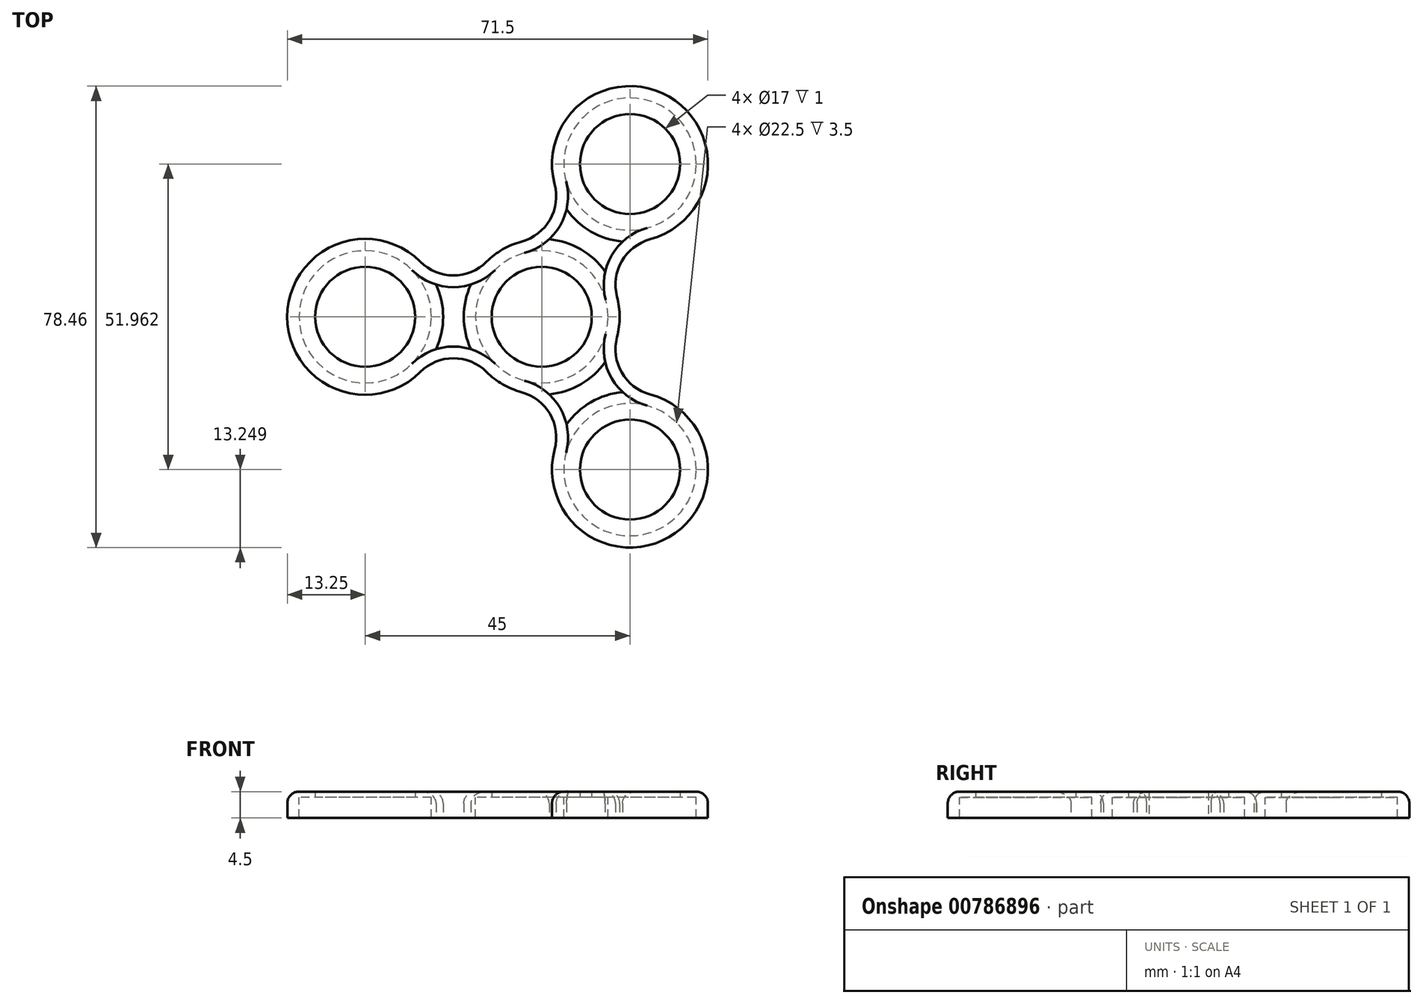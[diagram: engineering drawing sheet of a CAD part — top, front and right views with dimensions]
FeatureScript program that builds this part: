
annotation { "Feature Type Name" : "Feature", "Feature Type Description" : "" }
export const myFeature = defineFeature(function(context is Context, id is Id, definition is map)
    precondition{}
    {
        {
            assignVariable(context, id + "F0", {"name" : "B608_T", "anyValue" : 7});
        }
        {
            var Q0;
            Q0=qCreatedBy(makeId("Top.planeOp"),FACE);
            var sketch = newSketch(context, id + "F1", { "sketchPlane" : qUnion([Q0])});
            skCircle(sketch, "E0", {"center": v(0, 0) * mm, "radius": 11.25 * mm});
            skCircle(sketch, "E1.cCircle", {"center": v(0, 0) * mm, "radius": 15 * mm, "construction": true});
            skLineSegment(sketch, "E1.0", {"start": v(15, 25.98) * mm, "end": v(15, -25.98) * mm, "construction": true});
            skLineSegment(sketch, "E1.1", {"start": v(15, -25.98) * mm, "end": v(-30, 0) * mm, "construction": true});
            skLineSegment(sketch, "E1.2", {"start": v(-30, 0) * mm, "end": v(15, 25.98) * mm, "construction": true});
            skPoint(sketch, "E1.0.midPoint", {"position": v(15, 0) * mm});
            skCircle(sketch, "E2", {"center": v(-30, 0) * mm, "radius": 11.25 * mm});
            skCircle(sketch, "E3", {"center": v(15, -25.98) * mm, "radius": 11.25 * mm});
            skCircle(sketch, "E4", {"center": v(15, 25.98) * mm, "radius": 11.25 * mm});
            skPoint(sketch, "E5.orphan", {"position": v(0, -11.15) * mm});
            skPoint(sketch, "E6.orphan", {"position": v(0, 11.15) * mm});
            skArc(sketch, "E7.0", {"start": v(-17.94, -5.5) * mm, "mid": v(-16.75, 0) * mm, "end": v(-17.94, 5.5) * mm});
            skArc(sketch, "E8.0", {"start": v(2.2, -22.57) * mm, "mid": v(21.62, -37.46) * mm, "end": v(18.45, -13.19) * mm});
            skArc(sketch, "E9.0", {"start": v(18.45, 13.19) * mm, "mid": v(13.9, 39.18) * mm, "end": v(13.73, 12.8) * mm});
            skArc(sketch, "E10.0", {"start": v(-9.35, -9.39) * mm, "mid": v(-6.62, -11.47) * mm, "end": v(-3.45, -12.8) * mm});
            skLineSegment(sketch, "E11", {"start": v(-7.65, -13.25) * mm, "end": v(-7.03, -13.25) * mm});
            skLineSegment(sketch, "E12", {"start": v(-7.65, 13.25) * mm, "end": v(-7.03, 13.25) * mm});
            skLineSegment(sketch, "E13", {"start": v(-7.65, -13.25) * mm, "end": v(-7.96, -12.71) * mm});
            skLineSegment(sketch, "E14", {"start": v(15.3, 0) * mm, "end": v(15, 0.54) * mm});
            skLineSegment(sketch, "E15", {"start": v(-7.96, 12.71) * mm, "end": v(-7.65, 13.25) * mm});
            skLineSegment(sketch, "E16", {"start": v(15, -0.54) * mm, "end": v(15.3, 0) * mm});
            skPoint(sketch, "E17.orphan", {"position": v(0, -13.25) * mm});
            skPoint(sketch, "E18.orphan", {"position": v(0, 13.25) * mm});
            skCircle(sketch, "E19", {"center": v(0, 0) * mm, "radius": 8.5 * mm});
            skCircle(sketch, "E20", {"center": v(-30, 0) * mm, "radius": 8.5 * mm});
            skCircle(sketch, "E21", {"center": v(15, -25.98) * mm, "radius": 8.5 * mm});
            skCircle(sketch, "E22", {"center": v(15, 25.98) * mm, "radius": 8.5 * mm});
            skArc(sketch, "E23", {"start": v(-20.65, 9.39) * mm, "mid": v(-15, 7.05) * mm, "end": v(-9.35, 9.39) * mm});
            skArc(sketch, "E24", {"start": v(-9.35, -9.39) * mm, "mid": v(-15, -7.05) * mm, "end": v(-20.65, -9.39) * mm});
            skArc(sketch, "E25", {"start": v(-3.45, 12.8) * mm, "mid": v(1.4, 16.52) * mm, "end": v(2.2, 22.57) * mm});
            skArc(sketch, "E26", {"start": v(18.45, 13.19) * mm, "mid": v(13.6, 9.46) * mm, "end": v(12.8, 3.4) * mm});
            skArc(sketch, "E27", {"start": v(12.8, -3.4) * mm, "mid": v(13.6, -9.46) * mm, "end": v(18.45, -13.19) * mm});
            skArc(sketch, "E28", {"start": v(2.2, -22.57) * mm, "mid": v(1.4, -16.52) * mm, "end": v(-3.45, -12.8) * mm});
            skPoint(sketch, "E29.orphan", {"position": v(-30, 13.25) * mm});
            skPoint(sketch, "E30.orphan", {"position": v(-30, -13.25) * mm});
            skArc(sketch, "E31.0", {"start": v(-12.06, -5.5) * mm, "mid": v(-15, -5.05) * mm, "end": v(-17.94, -5.5) * mm});
            skArc(sketch, "E32.0", {"start": v(-17.94, 5.5) * mm, "mid": v(-15, 5.05) * mm, "end": v(-12.06, 5.5) * mm});
            skArc(sketch, "E33.trimOffspring", {"start": v(-12.06, 5.5) * mm, "mid": v(-13.25, 0) * mm, "end": v(-12.06, -5.5) * mm});
            skArc(sketch, "E34.trimOffspring", {"start": v(-20.65, 9.39) * mm, "mid": v(-43.25, 0) * mm, "end": v(-20.65, -9.39) * mm});
            skArc(sketch, "E35.trimOffspring", {"start": v(4.21, -18.29) * mm, "mid": v(3.12, -15.52) * mm, "end": v(1.27, -13.19) * mm});
            skArc(sketch, "E36.0", {"start": v(10.79, -7.7) * mm, "mid": v(11.88, -10.46) * mm, "end": v(13.73, -12.8) * mm});
            skArc(sketch, "E37.trimOffspring", {"start": v(1.27, -13.19) * mm, "mid": v(6.63, -11.47) * mm, "end": v(10.79, -7.7) * mm});
            skArc(sketch, "E38.trimOffspring", {"start": v(13.73, -12.8) * mm, "mid": v(8.38, -14.5) * mm, "end": v(4.21, -18.29) * mm});
            skArc(sketch, "E39.trimOffspring", {"start": v(12.8, -3.4) * mm, "mid": v(13.25, 0) * mm, "end": v(12.8, 3.4) * mm});
            skArc(sketch, "E40.0", {"start": v(1.27, 13.19) * mm, "mid": v(3.12, 15.52) * mm, "end": v(4.21, 18.29) * mm});
            skArc(sketch, "E41.trimOffspring", {"start": v(10.79, 7.7) * mm, "mid": v(6.62, 11.47) * mm, "end": v(1.27, 13.19) * mm});
            skArc(sketch, "E42.trimOffspring", {"start": v(13.73, 12.8) * mm, "mid": v(11.88, 10.46) * mm, "end": v(10.79, 7.7) * mm});
            skArc(sketch, "E43.trimOffspring", {"start": v(-3.45, 12.8) * mm, "mid": v(-6.63, 11.47) * mm, "end": v(-9.35, 9.39) * mm});
            skSolve(sketch);
        }
        {
            var Q0;
            Q0=makeQuery(id+"F1.imprint","IMPRINT",FACE,{"disambiguationData":[TD([[makeQuery(id+"F1.imprint","IMPRINT",EDGE,{"derivedFrom":sQuery(id+"F1.wireOp",EDGE,"E10.0")}),-1.0]])]});
            var Q1;
            Q1=makeQuery(id+"F1.imprint","IMPRINT",FACE,{"disambiguationData":[TD([[makeQuery(id+"F1.imprint","IMPRINT",EDGE,{"derivedFrom":sQuery(id+"F1.wireOp",EDGE,"E2")}),-1.0]])]});
            var Q2;
            Q2=makeQuery(id+"F1.imprint","IMPRINT",FACE,{"disambiguationData":[TD([[makeQuery(id+"F1.imprint","IMPRINT",EDGE,{"derivedFrom":sQuery(id+"F1.wireOp",EDGE,"E2")}),1.0]])]});
            var Q3;
            Q3=makeQuery(id+"F1.imprint","IMPRINT",FACE,{"disambiguationData":[TD([[makeQuery(id+"F1.imprint","IMPRINT",EDGE,{"derivedFrom":sQuery(id+"F1.wireOp",EDGE,"E0")}),-1.0]])]});
            var Q4;
            Q4=makeQuery(id+"F1.imprint","IMPRINT",FACE,{"disambiguationData":[TD([[makeQuery(id+"F1.imprint","IMPRINT",EDGE,{"derivedFrom":sQuery(id+"F1.wireOp",EDGE,"E0")}),1.0]])]});
            var Q5;
            Q5=makeQuery(id+"F1.imprint","IMPRINT",FACE,{"disambiguationData":[TD([[makeQuery(id+"F1.imprint","IMPRINT",EDGE,{"derivedFrom":sQuery(id+"F1.wireOp",EDGE,"E4")}),-1.0]])]});
            var Q6;
            Q6=makeQuery(id+"F1.imprint","IMPRINT",FACE,{"disambiguationData":[TD([[makeQuery(id+"F1.imprint","IMPRINT",EDGE,{"derivedFrom":sQuery(id+"F1.wireOp",EDGE,"E4")}),1.0]])]});
            var Q7;
            Q7=makeQuery(id+"F1.imprint","IMPRINT",FACE,{"disambiguationData":[TD([[makeQuery(id+"F1.imprint","IMPRINT",EDGE,{"derivedFrom":sQuery(id+"F1.wireOp",EDGE,"E3")}),-1.0]])]});
            var Q8;
            Q8=makeQuery(id+"F1.imprint","IMPRINT",FACE,{"disambiguationData":[TD([[makeQuery(id+"F1.imprint","IMPRINT",EDGE,{"derivedFrom":sQuery(id+"F1.wireOp",EDGE,"E3")}),1.0]])]});
            extrude(context, id + "F2", {"entities" : qUnion([Q0, Q1, Q2, Q3, Q4, Q5, Q6, Q7, Q8]), "depth" : 1 * mm, "offsetDistance" : 25 * mm});
        }
        {
            var Q0;
            Q0=makeQuery(id+"F1.imprint","IMPRINT",FACE,{"disambiguationData":[TD([[makeQuery(id+"F1.imprint","IMPRINT",EDGE,{"derivedFrom":sQuery(id+"F1.wireOp",EDGE,"E2")}),-1.0]])]});
            var Q1;
            Q1=makeQuery(id+"F1.imprint","IMPRINT",FACE,{"disambiguationData":[TD([[makeQuery(id+"F1.imprint","IMPRINT",EDGE,{"derivedFrom":sQuery(id+"F1.wireOp",EDGE,"E3")}),-1.0]])]});
            var Q2;
            Q2=makeQuery(id+"F1.imprint","IMPRINT",FACE,{"disambiguationData":[TD([[makeQuery(id+"F1.imprint","IMPRINT",EDGE,{"derivedFrom":sQuery(id+"F1.wireOp",EDGE,"E4")}),-1.0]])]});
            var Q3;
            Q3=makeQuery(id+"F1.imprint","IMPRINT",FACE,{"disambiguationData":[TD([[makeQuery(id+"F1.imprint","IMPRINT",EDGE,{"derivedFrom":sQuery(id+"F1.wireOp",EDGE,"E0")}),-1.0]])]});
            extrude(context, id + "F3", {"entities" : qUnion([Q0, Q1, Q2, Q3]), "operationType" : NewBodyOperationType.ADD, "oppositeDirection" : true, "depth" : (getVariable(context, 'B608_T') / 2) * mm, "offsetDistance" : 25 * mm});
        }
        {
            var Q0;
            Q0=makeQuery(id+"F2.opExtrude","CAP_EDGE",EDGE,{"disambiguationData":[OSD([sQuery(id+"F1.wireOp",EDGE,"E8.0")])],"isStart":false});
            var Q1;
            Q1=makeQuery(id+"F2.opExtrude","CAP_EDGE",EDGE,{"disambiguationData":[OSD([sQuery(id+"F1.wireOp",EDGE,"E25")])],"isStart":false});
            var Q2;
            Q2=makeQuery(id+"F2.opExtrude","CAP_EDGE",EDGE,{"disambiguationData":[OSD([sQuery(id+"F1.wireOp",EDGE,"E23")])],"isStart":false});
            var Q3;
            Q3=makeQuery(id+"F2.opExtrude","CAP_EDGE",EDGE,{"disambiguationData":[OSD([sQuery(id+"F1.wireOp",EDGE,"E24")])],"isStart":false});
            var Q4;
            Q4=makeQuery(id+"F2.opExtrude","CAP_EDGE",EDGE,{"disambiguationData":[OSD([sQuery(id+"F1.wireOp",EDGE,"E43.trimOffspring")])],"isStart":false});
            var Q5;
            Q5=makeQuery(id+"F2.opExtrude","CAP_EDGE",EDGE,{"disambiguationData":[OSD([sQuery(id+"F1.wireOp",EDGE,"E26")])],"isStart":false});
            var Q6;
            {var subQ0=sQuery(id+"F1.wireOp",EDGE,"E9.0");Q6=makeQuery(id+"F2.opExtrude","CAP_EDGE",EDGE,{"disambiguationData":[OSD([subQ0]),TDD([makeQuery(id+"F1.imprint","IMPRINT",EDGE,{"disambiguationData":[TD([[makeQuery(id+"F1.imprint","INTERSECT",VERTEX,{"derivedFrom":[subQ0,sQuery(id+"F1.wireOp",EDGE,"E26")]}),-1.0]])],"derivedFrom":subQ0})])],"isStart":false});}
            var Q7;
            Q7=makeQuery(id+"F2.opExtrude","CAP_EDGE",EDGE,{"disambiguationData":[OSD([sQuery(id+"F1.wireOp",EDGE,"E34.trimOffspring")])],"isStart":false});
            var Q8;
            Q8=makeQuery(id+"F2.opExtrude","CAP_EDGE",EDGE,{"disambiguationData":[OSD([sQuery(id+"F1.wireOp",EDGE,"E28")])],"isStart":false});
            var Q9;
            Q9=makeQuery(id+"F2.opExtrude","CAP_EDGE",EDGE,{"disambiguationData":[OSD([sQuery(id+"F1.wireOp",EDGE,"E10.0")])],"isStart":false});
            var Q10;
            Q10=makeQuery(id+"F2.opExtrude","CAP_EDGE",EDGE,{"disambiguationData":[OSD([sQuery(id+"F1.wireOp",EDGE,"E27")])],"isStart":false});
            var Q11;
            Q11=makeQuery(id+"F2.opExtrude","CAP_EDGE",EDGE,{"disambiguationData":[OSD([sQuery(id+"F1.wireOp",EDGE,"E39.trimOffspring")])],"isStart":false});
            fillet(context, id + "F4", {"entities" : qUnion([Q0, Q1, Q2, Q3, Q4, Q5, Q6, Q7, Q8, Q9, Q10, Q11]), "radius" : 2 * mm, "tangentPropagation" : true, "allowEdgeOverflow" : false});
        }
        {
            var Q0;
            Q0=makeQuery(id+"F2.opExtrude","CAP_EDGE",EDGE,{"disambiguationData":[OSD([sQuery(id+"F1.wireOp",EDGE,"E41.trimOffspring")])],"isStart":false});
            var Q1;
            Q1=makeQuery(id+"F2.opExtrude","CAP_EDGE",EDGE,{"disambiguationData":[OSD([sQuery(id+"F1.wireOp",EDGE,"E37.trimOffspring")])],"isStart":false});
            var Q2;
            Q2=makeQuery(id+"F2.opExtrude","CAP_EDGE",EDGE,{"disambiguationData":[OSD([sQuery(id+"F1.wireOp",EDGE,"E33.trimOffspring")])],"isStart":false});
            var Q3;
            {var subQ0=sQuery(id+"F1.wireOp",EDGE,"E9.0");Q3=makeQuery(id+"F2.opExtrude","CAP_EDGE",EDGE,{"disambiguationData":[OSD([subQ0]),TDD([makeQuery(id+"F1.imprint","IMPRINT",EDGE,{"disambiguationData":[TD([[makeQuery(id+"F1.imprint","INTERSECT",VERTEX,{"derivedFrom":[subQ0,sQuery(id+"F1.wireOp",EDGE,"E42.trimOffspring")]}),1.0]])],"derivedFrom":subQ0})])],"isStart":false});}
            var Q4;
            Q4=makeQuery(id+"F2.opExtrude","CAP_EDGE",EDGE,{"disambiguationData":[OSD([sQuery(id+"F1.wireOp",EDGE,"E7.0")])],"isStart":false});
            var Q5;
            Q5=makeQuery(id+"F2.opExtrude","CAP_EDGE",EDGE,{"disambiguationData":[OSD([sQuery(id+"F1.wireOp",EDGE,"E38.trimOffspring")])],"isStart":false});
            fillet(context, id + "F5", {"entities" : qUnion([Q0, Q1, Q2, Q3, Q4, Q5]), "radius" : 2 * mm, "tangentPropagation" : true, "allowEdgeOverflow" : false});
        }
    });
